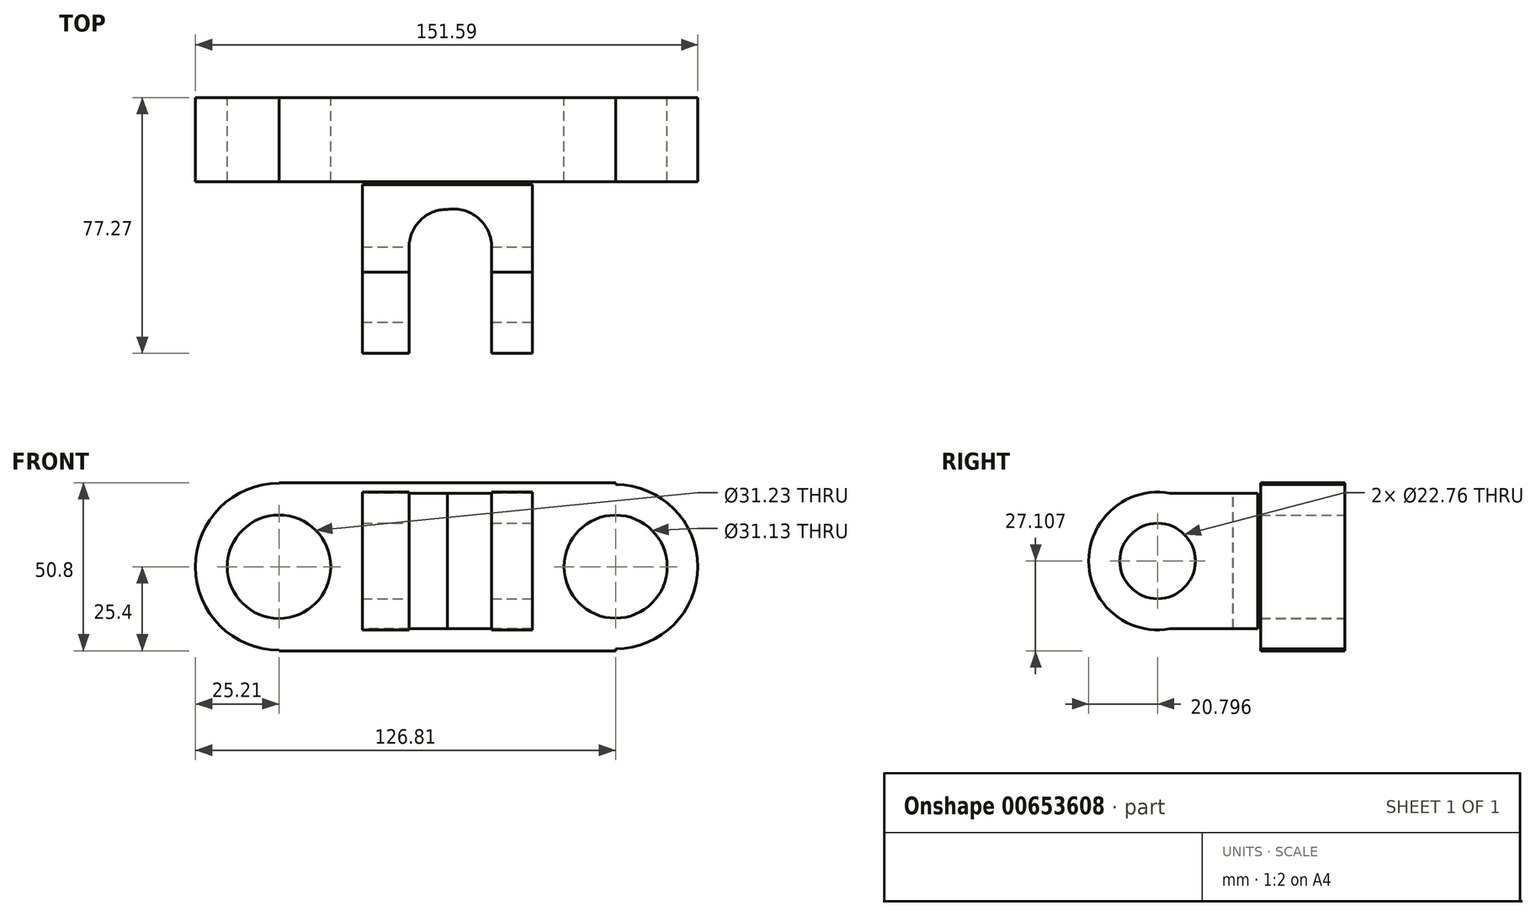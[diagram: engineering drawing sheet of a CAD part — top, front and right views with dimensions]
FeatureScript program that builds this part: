
annotation { "Feature Type Name" : "Feature", "Feature Type Description" : "" }
export const myFeature = defineFeature(function(context is Context, id is Id, definition is map)
    precondition{}
    {
        {
            var Q0;
            Q0=qCreatedBy(makeId("Front.planeOp"),FACE);
            var sketch = newSketch(context, id + "F0", { "sketchPlane" : qUnion([Q0])});
            skLineSegment(sketch, "E0.bottom", {"start": v(50.8, -25.4) * mm, "end": v(-50.8, -25.4) * mm});
            skLineSegment(sketch, "E0.top", {"start": v(50.8, 25.4) * mm, "end": v(-50.8, 25.4) * mm});
            skLineSegment(sketch, "E0.left", {"start": v(50.8, -25.4) * mm, "end": v(50.8, -24.78) * mm});
            skLineSegment(sketch, "E0.right", {"start": v(-50.8, -25.4) * mm, "end": v(-50.8, -25.21) * mm});
            skPoint(sketch, "E0.middle", {"position": v(0, 0) * mm});
            skArc(sketch, "E1", {"start": v(-50.8, 25.21) * mm, "mid": v(-76.01, 0) * mm, "end": v(-50.8, -25.21) * mm});
            skArc(sketch, "E2", {"start": v(50.8, -24.78) * mm, "mid": v(75.58, 0) * mm, "end": v(50.8, 24.78) * mm});
            skLineSegment(sketch, "E3.trimOffspring", {"start": v(-50.8, 25.21) * mm, "end": v(-50.8, 25.4) * mm});
            skLineSegment(sketch, "E4.trimOffspring", {"start": v(50.8, 24.78) * mm, "end": v(50.8, 25.4) * mm});
            skCircle(sketch, "E5", {"center": v(-50.8, 0) * mm, "radius": 15.62 * mm});
            skCircle(sketch, "E6", {"center": v(50.8, 0) * mm, "radius": 15.57 * mm});
            skSolve(sketch);
        }
        {
            var Q0;
            Q0=makeQuery(id+"F0.imprint","IMPRINT",FACE,{"disambiguationData":[TD([[makeQuery(id+"F0.imprint","IMPRINT",EDGE,{"derivedFrom":sQuery(id+"F0.wireOp",EDGE,"E0.bottom")}),-1.0]])]});
            extrude(context, id + "F1", {"entities" : qUnion([Q0]), "depth" : 25.4 * mm, "offsetDistance" : 25.4 * mm});
        }
        {
            var Q0;
            Q0=qCreatedBy(makeId("Right.planeOp"),FACE);
            var sketch = newSketch(context, id + "F2", { "sketchPlane" : qUnion([Q0])});
            skLineSegment(sketch, "E7.bottom", {"start": v(-26.24, 22.17) * mm, "end": v(-56.47, 22.17) * mm});
            skLineSegment(sketch, "E7.top", {"start": v(-26.24, -18.75) * mm, "end": v(-56.47, -18.75) * mm});
            skLineSegment(sketch, "E7.left", {"start": v(-26.24, 22.17) * mm, "end": v(-26.24, -18.75) * mm});
            skArc(sketch, "E8", {"start": v(-52.75, 22.17) * mm, "mid": v(-77.27, 1.7) * mm, "end": v(-52.75, -18.75) * mm});
            skSolve(sketch);
        }
        {
            var Q0;
            {var subQ0=sQuery(id+"F2.wireOp",EDGE,"E7.left");Q0=makeQuery(id+"F2.imprint","IMPRINT",FACE,{"disambiguationData":[TD([[makeQuery(id+"F2.imprint","IMPRINT",EDGE,{"derivedFrom":subQ0}),-1.0]])]});}
            extrude(context, id + "F3", {"entities" : qUnion([Q0]), "endBound" : BoundingType.SYMMETRIC, "depth" : 51.3 * mm, "offsetDistance" : 25.4 * mm});
        }
        {
            var Q0;
            Q0=makeQuery(id+"F3.opExtrude","SWEPT_FACE",FACE,{"disambiguationData":[OSD([sQuery(id+"F2.wireOp",EDGE,"E7.bottom")])]});
            var sketch = newSketch(context, id + "F4", { "sketchPlane" : qUnion([Q0])});
            skLineSegment(sketch, "E9", {"start": v(13.38, -77.42) * mm, "end": v(13.38, -45.13) * mm});
            skLineSegment(sketch, "E10", {"start": v(-11.53, -45.13) * mm, "end": v(-11.53, -78.34) * mm});
            skArc(sketch, "E11", {"start": v(0, -33.75) * mm, "mid": v(-8.15, -37.03) * mm, "end": v(-11.53, -45.13) * mm});
            skArc(sketch, "E12", {"start": v(13.38, -45.13) * mm, "mid": v(9.32, -36.35) * mm, "end": v(0, -33.75) * mm});
            skLineSegment(sketch, "E13", {"start": v(13.38, -77.42) * mm, "end": v(-11.53, -78.34) * mm});
            skSolve(sketch);
        }
        {
            var Q0;
            {var subQ1=sQuery(id+"F4.wireOp",EDGE,"E11");Q0=makeQuery(id+"F4.imprint","IMPRINT",FACE,{"disambiguationData":[TD([[makeQuery(id+"F4.imprint","IMPRINT",EDGE,{"derivedFrom":subQ1}),1.0]])]});}
            var Q1;
            {var subQ0=sQuery(id+"F4.wireOp",EDGE,"E13");Q1=makeQuery(id+"F4.imprint","IMPRINT",FACE,{"disambiguationData":[TD([[makeQuery(id+"F4.imprint","IMPRINT",EDGE,{"derivedFrom":subQ0}),-1.0]])]});}
            extrude(context, id + "F5", {"entities" : qUnion([Q0, Q1]), "operationType" : NewBodyOperationType.REMOVE, "endBound" : BoundingType.SYMMETRIC, "oppositeDirection" : true, "depth" : 108.7 * mm, "offsetDistance" : 25.4 * mm});
        }
        {
            var Q0;
            Q0=makeQuery(id+"F3.opExtrude","CAP_FACE",FACE,{"disambiguationData":[OSD([sQuery(id+"F2.wireOp",EDGE,"E7.bottom"),sQuery(id+"F2.wireOp",EDGE,"E7.top"),sQuery(id+"F2.wireOp",EDGE,"E7.left"),sQuery(id+"F2.wireOp",EDGE,"E8")])],"isStart":false});
            var sketch = newSketch(context, id + "F6", { "sketchPlane" : qUnion([Q0])});
            skCircle(sketch, "E14", {"center": v(-56.47, 1.7) * mm, "radius": 11.38 * mm});
            skSolve(sketch);
        }
        {
            var Q0;
            Q0 = qSketchRegion(id + "F6", true);
            extrude(context, id + "F7", {"entities" : qUnion([Q0]), "operationType" : NewBodyOperationType.REMOVE, "oppositeDirection" : true, "depth" : 94.23 * mm, "offsetDistance" : 25.4 * mm});
        }
    });
